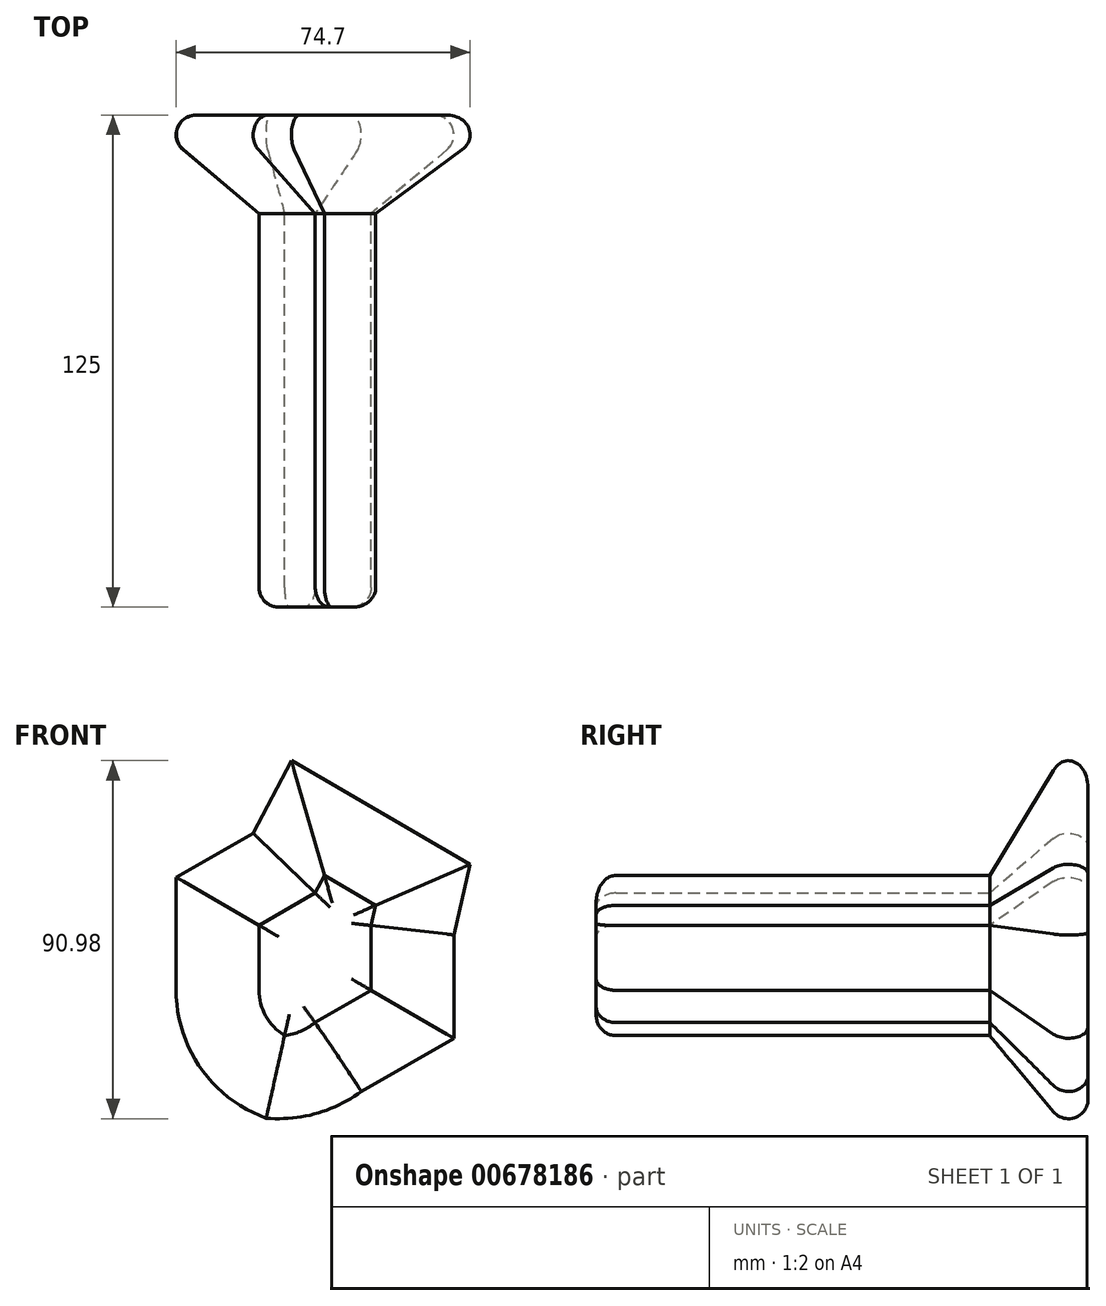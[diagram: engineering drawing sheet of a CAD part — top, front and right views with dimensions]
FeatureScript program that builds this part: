
annotation { "Feature Type Name" : "Feature", "Feature Type Description" : "" }
export const myFeature = defineFeature(function(context is Context, id is Id, definition is map)
    precondition{}
    {
        {
            var Q0;
            Q0=qCreatedBy(makeId("Front.planeOp"),FACE);
            var sketch = newSketch(context, id + "F0", { "sketchPlane" : qUnion([Q0])});
            skLineSegment(sketch, "E0.0", {"start": v(13.38, -9.48) * mm, "end": v(-0.87, -17.67) * mm});
            skLineSegment(sketch, "E0.1", {"start": v(-0.87, -17.67) * mm, "end": v(-15.09, -9.42) * mm});
            skLineSegment(sketch, "E0.2", {"start": v(-15.09, -9.42) * mm, "end": v(-15.06, 7.02) * mm});
            skLineSegment(sketch, "E0.3", {"start": v(-15.06, 7.02) * mm, "end": v(-0.8, 15.2) * mm});
            skLineSegment(sketch, "E0.4", {"start": v(-0.8, 15.2) * mm, "end": v(13.42, 6.96) * mm});
            skLineSegment(sketch, "E0.5", {"start": v(13.42, 6.96) * mm, "end": v(13.38, -9.48) * mm});
            skLineSegment(sketch, "E1", {"start": v(-0.8, 15.2) * mm, "end": v(1.55, 19.66) * mm});
            skLineSegment(sketch, "E2", {"start": v(1.55, 19.66) * mm, "end": v(14.59, 12.1) * mm});
            skLineSegment(sketch, "E3", {"start": v(14.59, 12.1) * mm, "end": v(13.42, 6.96) * mm});
            skArc(sketch, "E4", {"start": v(-8.6, -20.97) * mm, "mid": v(-4.48, -19.9) * mm, "end": v(-0.87, -17.67) * mm});
            skArc(sketch, "E5", {"start": v(-15.09, -9.42) * mm, "mid": v(-13.36, -16.05) * mm, "end": v(-8.6, -20.97) * mm});
            skSolve(sketch);
        }
        {
            var Q0;
            Q0=makeQuery(id+"F0.imprint","IMPRINT",FACE,{"disambiguationData":[TD([[makeQuery(id+"F0.imprint","IMPRINT",EDGE,{"derivedFrom":sQuery(id+"F0.wireOp",EDGE,"E0.0")}),-1.0]])]});
            var Q1;
            Q1=makeQuery(id+"F0.imprint","IMPRINT",FACE,{"disambiguationData":[TD([[makeQuery(id+"F0.imprint","IMPRINT",EDGE,{"derivedFrom":sQuery(id+"F0.wireOp",EDGE,"E0.4")}),1.0]])]});
            var Q2;
            Q2=makeQuery(id+"F0.imprint","IMPRINT",FACE,{"disambiguationData":[TD([[makeQuery(id+"F0.imprint","IMPRINT",EDGE,{"derivedFrom":sQuery(id+"F0.wireOp",EDGE,"E0.1")}),1.0]])]});
            extrude(context, id + "F1", {"entities" : qUnion([Q0, Q1, Q2]), "depth" : 100 * mm, "offsetDistance" : 25 * mm});
        }
        {
            var Q0;
            Q0=makeQuery(id+"F1.opExtrude","CAP_FACE",FACE,{"disambiguationData":[OSD([sQuery(id+"F0.wireOp",EDGE,"E0.0"),sQuery(id+"F0.wireOp",EDGE,"E0.2"),sQuery(id+"F0.wireOp",EDGE,"E0.3"),sQuery(id+"F0.wireOp",EDGE,"E0.5"),sQuery(id+"F0.wireOp",EDGE,"E1"),sQuery(id+"F0.wireOp",EDGE,"E2"),sQuery(id+"F0.wireOp",EDGE,"E3"),sQuery(id+"F0.wireOp",EDGE,"E4"),sQuery(id+"F0.wireOp",EDGE,"E5")])],"isStart":true});
            extrude(context, id + "F2", {"entities" : qUnion([Q0]), "operationType" : NewBodyOperationType.ADD, "depth" : 25 * mm, "offsetDistance" : 25 * mm, "hasDraft" : true, "draftAngle" : 50 * degree});
        }
        {
            var Q0;
            Q0=makeQuery(id+"F1.opExtrude","CAP_FACE",FACE,{"disambiguationData":[OSD([sQuery(id+"F0.wireOp",EDGE,"E0.0"),sQuery(id+"F0.wireOp",EDGE,"E0.2"),sQuery(id+"F0.wireOp",EDGE,"E0.3"),sQuery(id+"F0.wireOp",EDGE,"E0.5"),sQuery(id+"F0.wireOp",EDGE,"E1"),sQuery(id+"F0.wireOp",EDGE,"E2"),sQuery(id+"F0.wireOp",EDGE,"E3"),sQuery(id+"F0.wireOp",EDGE,"E4"),sQuery(id+"F0.wireOp",EDGE,"E5")])],"isStart":false});
            fillet(context, id + "F3", {"entities" : qUnion([Q0]), "radius" : 5 * mm, "tangentPropagation" : true, "allowEdgeOverflow" : false});
        }
        {
            var Q0;
            Q0=makeQuery(id+"F2.opExtrude","CAP_FACE",FACE,{"disambiguationData":[OSD([sQuery(id+"F0.wireOp",EDGE,"E0.0"),sQuery(id+"F0.wireOp",EDGE,"E0.2"),sQuery(id+"F0.wireOp",EDGE,"E0.3"),sQuery(id+"F0.wireOp",EDGE,"E0.5"),sQuery(id+"F0.wireOp",EDGE,"E1"),sQuery(id+"F0.wireOp",EDGE,"E2"),sQuery(id+"F0.wireOp",EDGE,"E3"),sQuery(id+"F0.wireOp",EDGE,"E4"),sQuery(id+"F0.wireOp",EDGE,"E5")])],"isStart":false});
            fillet(context, id + "F4", {"entities" : qUnion([Q0]), "radius" : 5 * mm, "tangentPropagation" : true, "allowEdgeOverflow" : false});
        }
    });
